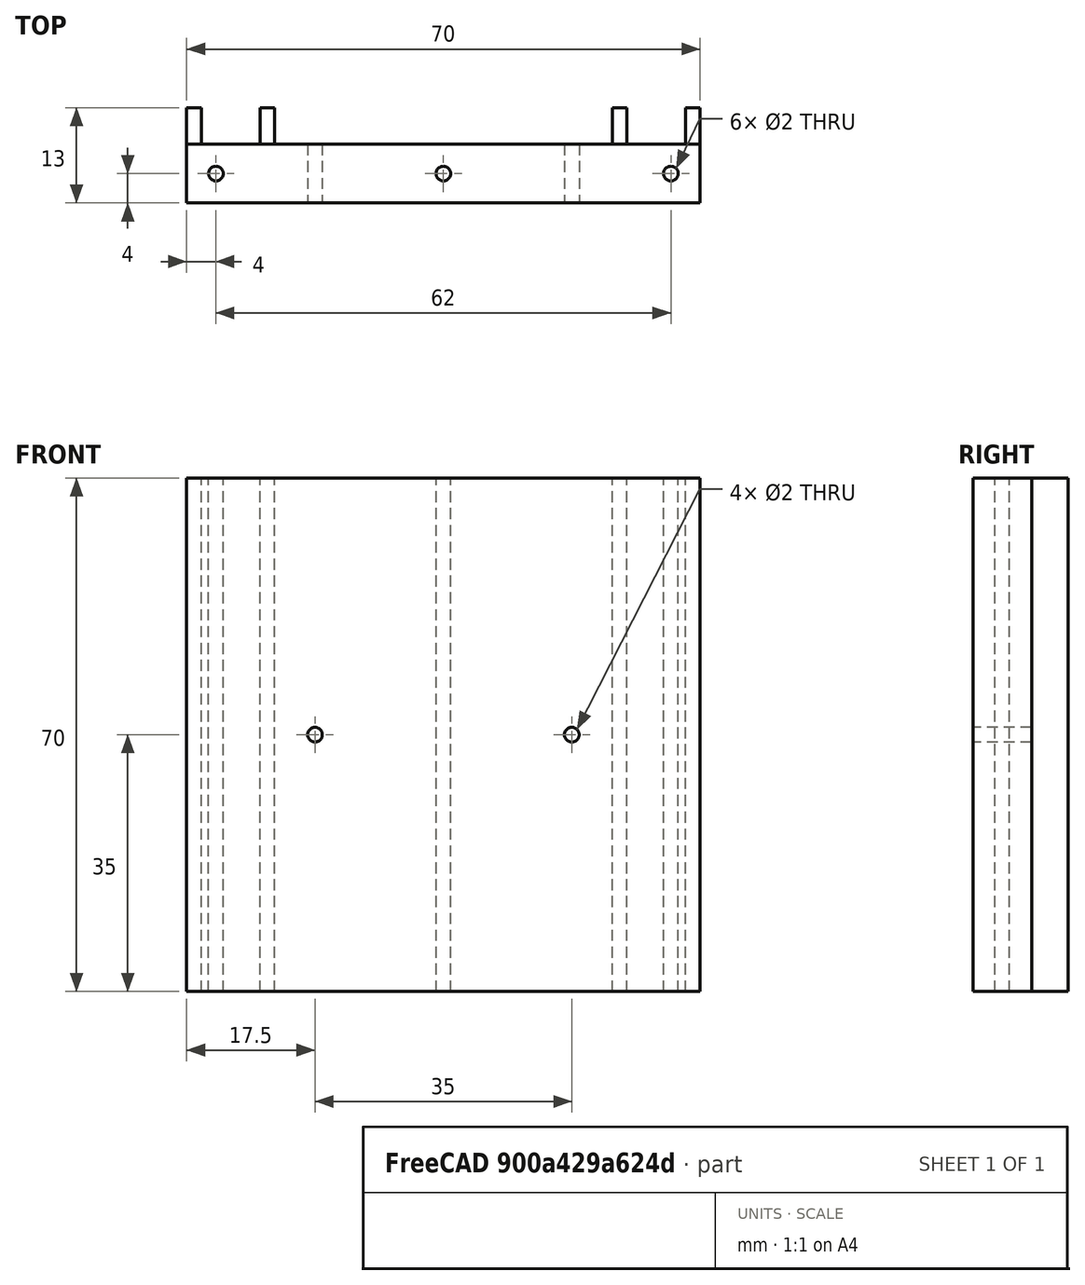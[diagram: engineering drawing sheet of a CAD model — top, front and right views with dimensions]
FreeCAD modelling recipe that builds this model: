
FCSTD DOCUMENT  (FreeCAD 0.18R16146 (Git))
Label: sides
License: All rights reserved
LicenseURL: http://en.wikipedia.org/wiki/All_rights_reserved
objects: Part::Cylinder×10, Part::Box×10, Part::Cut×10, Part::MultiFuse×1
note: 31 computed .brp shape members not serialized (recipe doc carries the construction recipe); baked Part::Feature solids carry a one-line shape summary decoded from their .brp

FEATURE [Part::Cylinder] Cylinder003  label="Zylinder003"
  Angle = 360
  AttacherType = Attacher::AttachEngine3D
  Height = 8
  Placement = pos=(18.5,9,35) rot=(1,0,0;1.5708rad)
  Radius = 1
FEATURE [Part::Box] Box008  label="Würfel008"
  AttacherType = Attacher::AttachEngine3D
  Height = 70
  Length = 2
  Placement = pos=(1,9,0) rot=(0,0,1;0rad)
  Width = 5
FEATURE [Part::Box] Box  label="Würfel"
  AttacherType = Attacher::AttachEngine3D
  Height = 70
  Length = 2
  Placement = pos=(1,9,0) rot=(0,0,1;0rad)
  Width = 5
FEATURE [Part::Box] Box009  label="Würfel009"
  AttacherType = Attacher::AttachEngine3D
  Height = 70
  Length = 2
  Placement = pos=(11,9,0) rot=(0,0,1;0rad)
  Width = 5
FEATURE [Part::Box] Box003  label="Würfel003"
  AttacherType = Attacher::AttachEngine3D
  Height = 70
  Length = 2
  Placement = pos=(69,9,0) rot=(0,0,1;0rad)
  Width = 5
FEATURE [Part::Cylinder] Cylinder  label="Zylinder"
  Angle = 360
  AttacherType = Attacher::AttachEngine3D
  Height = 70
  Placement = pos=(36,5,0) rot=(0,0,1;0rad)
  Radius = 1
FEATURE [Part::Cylinder] Cylinder001  label="Zylinder001"
  Angle = 360
  AttacherType = Attacher::AttachEngine3D
  Height = 70
  Placement = pos=(5,5,0) rot=(0,0,1;0rad)
  Radius = 1
FEATURE [Part::Cylinder] Cylinder004  label="Zylinder004"
  Angle = 360
  AttacherType = Attacher::AttachEngine3D
  Height = 8
  Placement = pos=(53.5,9,35) rot=(1,0,0;1.5708rad)
  Radius = 1
FEATURE [Part::Box] Box001  label="Würfel001"
  AttacherType = Attacher::AttachEngine3D
  Height = 70
  Length = 70
  Placement = pos=(1,1,0) rot=(0,0,1;0rad)
  Width = 8
FEATURE [Part::Cylinder] Cylinder005  label="Zylinder005"
  Angle = 360
  AttacherType = Attacher::AttachEngine3D
  Height = 70
  Placement = pos=(36,5,0) rot=(0,0,1;0rad)
  Radius = 1
FEATURE [Part::Box] Box010  label="Würfel010"
  AttacherType = Attacher::AttachEngine3D
  Height = 70
  Length = 2
  Placement = pos=(69,9,0) rot=(0,0,1;0rad)
  Width = 5
FEATURE [Part::Cut] Cut
  Base = -> Box001
  Tool = -> Cylinder001
FEATURE [Part::Cylinder] Cylinder009  label="Zylinder009"
  Angle = 360
  AttacherType = Attacher::AttachEngine3D
  Height = 8
  Placement = pos=(53.5,9,35) rot=(1,0,0;1.5708rad)
  Radius = 1
FEATURE [Part::Box] Box011  label="Würfel011"
  AttacherType = Attacher::AttachEngine3D
  Height = 70
  Length = 2
  Placement = pos=(59,9,0) rot=(0,0,1;0rad)
  Width = 5
FEATURE [Part::Cylinder] Cylinder006  label="Zylinder006"
  Angle = 360
  AttacherType = Attacher::AttachEngine3D
  Height = 70
  Placement = pos=(67,5,0) rot=(0,0,1;0rad)
  Radius = 1
FEATURE [Part::Cylinder] Cylinder007  label="Zylinder007"
  Angle = 360
  AttacherType = Attacher::AttachEngine3D
  Height = 70
  Placement = pos=(5,5,0) rot=(0,0,1;0rad)
  Radius = 1
FEATURE [Part::Cylinder] Cylinder008  label="Zylinder008"
  Angle = 360
  AttacherType = Attacher::AttachEngine3D
  Height = 8
  Placement = pos=(18.5,9,35) rot=(1,0,0;1.5708rad)
  Radius = 1
FEATURE [Part::Box] Box004  label="Würfel004"
  AttacherType = Attacher::AttachEngine3D
  Height = 70
  Length = 2
  Placement = pos=(59,9,0) rot=(0,0,1;0rad)
  Width = 5
FEATURE [Part::Box] Box007  label="Würfel007"
  AttacherType = Attacher::AttachEngine3D
  Height = 70
  Length = 70
  Placement = pos=(1,1,0) rot=(0,0,1;0rad)
  Width = 8
FEATURE [Part::Cut] Cut005
  Base = -> Box007
  Tool = -> Cylinder007
FEATURE [Part::Cut] Cut009
  Base = -> Cut005
  Tool = -> Cylinder006
FEATURE [Part::Cut] Cut007
  Base = -> Cut009
  Tool = -> Cylinder005
FEATURE [Part::Cut] Cut006
  Base = -> Cut007
  Tool = -> Cylinder008
FEATURE [Part::Cut] Cut008
  Base = -> Cut006
  Tool = -> Cylinder009
FEATURE [Part::Cylinder] Cylinder002  label="Zylinder002"
  Angle = 360
  AttacherType = Attacher::AttachEngine3D
  Height = 70
  Placement = pos=(67,5,0) rot=(0,0,1;0rad)
  Radius = 1
FEATURE [Part::Cut] Cut001
  Base = -> Cut
  Tool = -> Cylinder002
FEATURE [Part::Cut] Cut002
  Base = -> Cut001
  Tool = -> Cylinder
FEATURE [Part::Cut] Cut003
  Base = -> Cut002
  Tool = -> Cylinder003
FEATURE [Part::Cut] Cut004
  Base = -> Cut003
  Tool = -> Cylinder004
FEATURE [Part::Box] Box002  label="Würfel002"
  AttacherType = Attacher::AttachEngine3D
  Height = 70
  Length = 2
  Placement = pos=(11,9,0) rot=(0,0,1;0rad)
  Width = 5
FEATURE [Part::MultiFuse] Fusion
  Shapes = -> [Box,Box003,Box004,Box002,Cut004]
